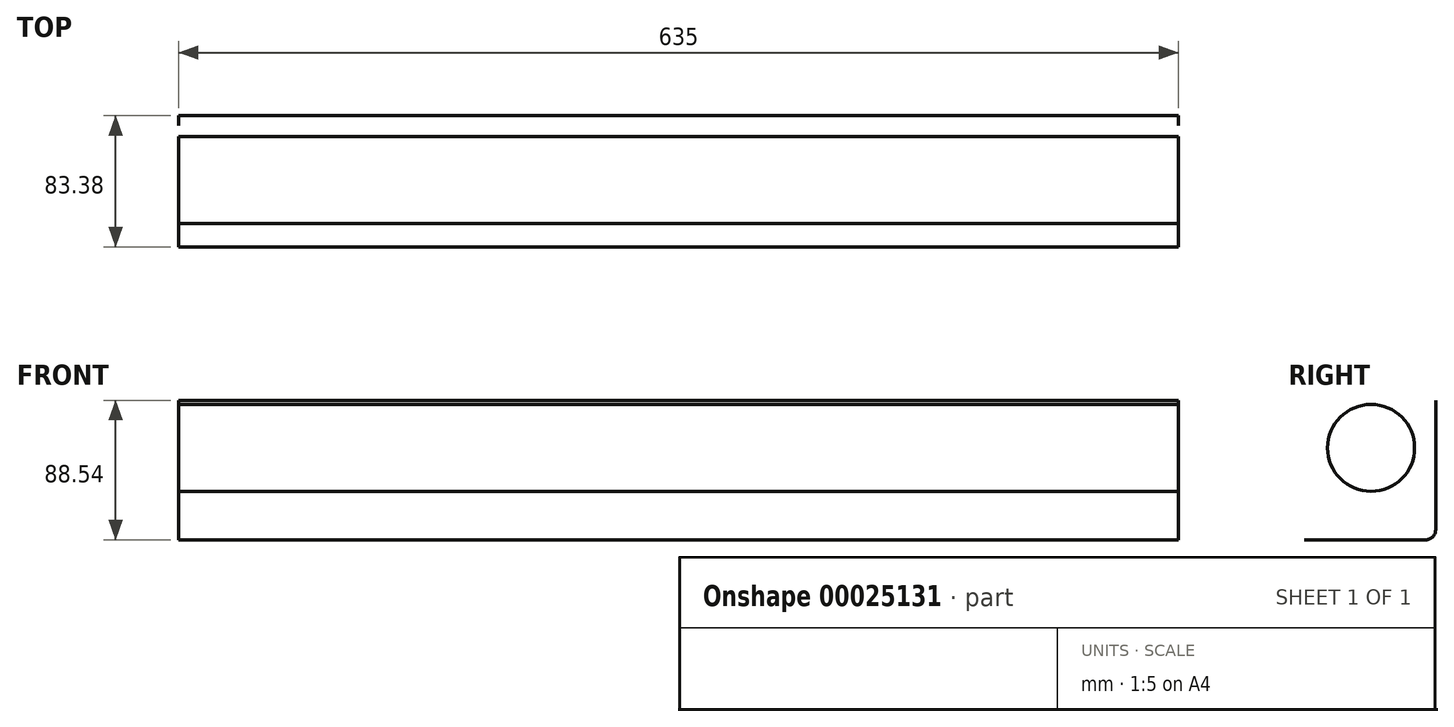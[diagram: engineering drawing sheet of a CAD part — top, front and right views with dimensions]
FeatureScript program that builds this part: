
annotation { "Feature Type Name" : "Feature", "Feature Type Description" : "" }
export const myFeature = defineFeature(function(context is Context, id is Id, definition is map)
    precondition{}
    {
        {
            var Q0;
            Q0=qCreatedBy(makeId("Right.planeOp"),FACE);
            var sketch = newSketch(context, id + "F0", { "sketchPlane" : qUnion([Q0])});
            skLineSegment(sketch, "E0.bottom", {"start": v(34.64, 36.5) * mm, "end": v(-42.4, 36.5) * mm});
            skLineSegment(sketch, "E0.top", {"start": v(34.64, -58.38) * mm, "end": v(-42.4, -58.38) * mm});
            skLineSegment(sketch, "E0.left", {"start": v(41, 30.16) * mm, "end": v(41, -52.03) * mm});
            skLineSegment(sketch, "E0.right", {"start": v(-48.74, 30.16) * mm, "end": v(-48.74, -52.03) * mm});
            skPoint(sketch, "E1.visualSharp", {"position": v(41, 36.5) * mm});
            skArc(sketch, "E1.filletArc", {"start": v(41, 30.16) * mm, "mid": v(39.13, 34.65) * mm, "end": v(34.64, 36.5) * mm});
            skPoint(sketch, "E2.visualSharp", {"position": v(41, -58.38) * mm});
            skArc(sketch, "E2.filletArc", {"start": v(34.64, -58.38) * mm, "mid": v(39.13, -56.52) * mm, "end": v(41, -52.03) * mm});
            skPoint(sketch, "E3.visualSharp", {"position": v(-48.74, -58.38) * mm});
            skArc(sketch, "E3.filletArc", {"start": v(-48.74, -52.03) * mm, "mid": v(-46.88, -56.52) * mm, "end": v(-42.4, -58.38) * mm});
            skPoint(sketch, "E4.visualSharp", {"position": v(-48.74, 36.5) * mm});
            skArc(sketch, "E4.filletArc", {"start": v(-42.4, 36.5) * mm, "mid": v(-46.88, 34.65) * mm, "end": v(-48.74, 30.16) * mm});
            skCircle(sketch, "E5", {"center": v(0, 0) * mm, "radius": 27.64 * mm});
            skSolve(sketch);
        }
        {
            var Q0;
            Q0=sQuery(id+"F0.wireOp",EDGE,"E0.left");
            var Q1;
            Q1=sQuery(id+"F0.wireOp",EDGE,"E5");
            var Q2;
            Q2=sQuery(id+"F0.wireOp",EDGE,"E2.filletArc");
            var Q3;
            Q3=sQuery(id+"F0.wireOp",EDGE,"E0.top");
            extrude(context, id + "F1", {"bodyType" : ToolBodyType.SURFACE, "surfaceEntities" : qUnion([Q0, Q1, Q2, Q3]), "depth" : 635 * mm});
        }
    });
